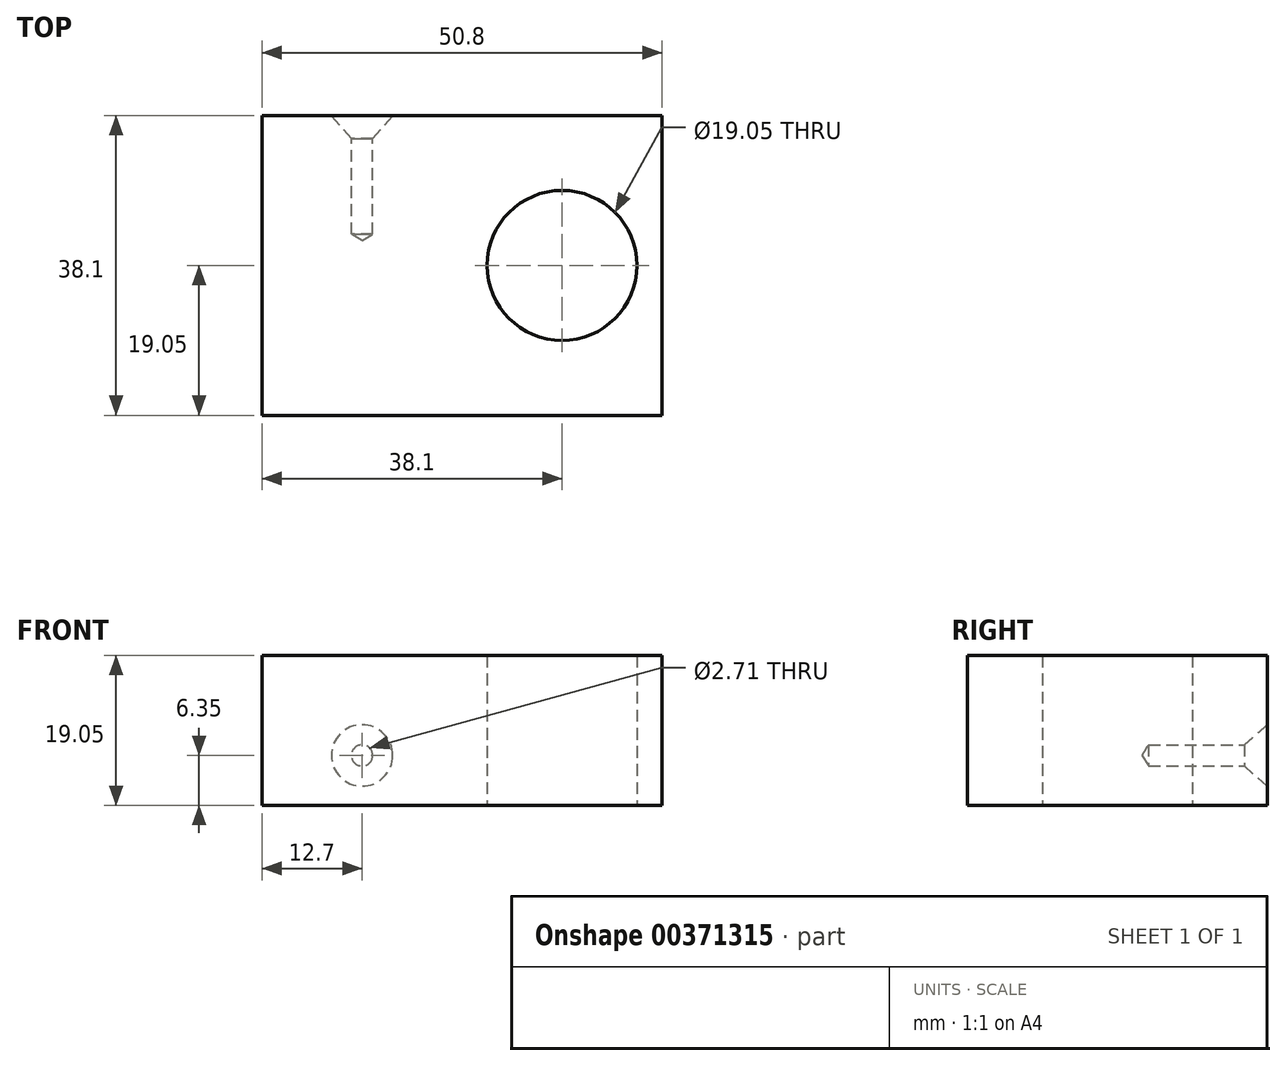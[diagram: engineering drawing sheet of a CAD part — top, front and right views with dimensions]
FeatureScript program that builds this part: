
annotation { "Feature Type Name" : "Feature", "Feature Type Description" : "" }
export const myFeature = defineFeature(function(context is Context, id is Id, definition is map)
    precondition{}
    {
        {
            var Q0;
            Q0=qCreatedBy(makeId("Top.planeOp"),FACE);
            var sketch = newSketch(context, id + "F0", { "sketchPlane" : qUnion([Q0])});
            skLineSegment(sketch, "E0.bottom", {"start": v(0, 38.1) * mm, "end": v(50.8, 38.1) * mm});
            skLineSegment(sketch, "E0.top", {"start": v(0, 0) * mm, "end": v(50.8, 0) * mm});
            skLineSegment(sketch, "E0.left", {"start": v(0, 38.1) * mm, "end": v(0, 0) * mm});
            skLineSegment(sketch, "E0.right", {"start": v(50.8, 38.1) * mm, "end": v(50.8, 0) * mm});
            skCircle(sketch, "E1", {"center": v(38.1, 19.05) * mm, "radius": 9.53 * mm});
            skSolve(sketch);
        }
        {
            var Q0;
            Q0=makeQuery(id+"F0.imprint","IMPRINT",FACE,{"disambiguationData":[TD([[makeQuery(id+"F0.imprint","IMPRINT",EDGE,{"derivedFrom":sQuery(id+"F0.wireOp",EDGE,"E0.bottom")}),-1.0]])]});
            extrude(context, id + "F1", {"entities" : qUnion([Q0]), "depth" : 19.05 * mm});
        }
        {
            var Q0;
            Q0=makeQuery(id+"F1.opExtrude","SWEPT_FACE",FACE,{"disambiguationData":[OSD([sQuery(id+"F0.wireOp",EDGE,"E0.bottom")])]});
            var sketch = newSketch(context, id + "F2", { "sketchPlane" : qUnion([Q0])});
            skPoint(sketch, "E2", {"position": v(-12.7, 6.35) * mm});
            skSolve(sketch);
        }
        {
            var Q0;
            Q0=sQuery(id+"F2.wireOp",VERTEX,"E2");
            var Q1;
            Q1=makeQuery(id+"F1.opExtrude","SWEPT_BODY",BODY,{"disambiguationData":[OSD([sQuery(id+"F0.wireOp",EDGE,"E0.bottom"),sQuery(id+"F0.wireOp",EDGE,"E0.top"),sQuery(id+"F0.wireOp",EDGE,"E0.left"),sQuery(id+"F0.wireOp",EDGE,"E0.right"),sQuery(id+"F0.wireOp",EDGE,"E1")])]});
            hole(context, id + "F3", {"style" : HoleStyle.C_SINK, "endStyle" : HoleEndStyle.BLIND, "standardTappedOrClearance" : lookupTablePath({ "standard" : "ANSI", "engagement" : "75%", "pitch" : "32 tpi", "size" : "#6", "type" : "Tapped" }), "standardBlindInLast" : lookupTablePath({ "standard" : "ANSI", "engagement" : "75%", "pitch" : "32 tpi", "size" : "#6", "type" : "Tapped" }), "holeDiameter" : 2.7 * mm, "cSinkDiameter" : 7.8 * mm, "cSinkAngle" : 82 * degree, "showTappedDepth" : true, "holeDepth" : 15.08 * mm, "isTappedThrough" : true, "tappedDepth" : 12.7 * mm, "tapClearance" : 3, "locations" : qUnion([Q0]), "scope" : qUnion([Q1]), "majorDiameter" : 3.5 * mm});
        }
    });
